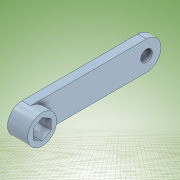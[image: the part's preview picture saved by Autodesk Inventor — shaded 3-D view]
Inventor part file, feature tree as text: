
AUTODESK INVENTOR PART (.ipt)
format: ipt  version: 2022 (Build 260153000, 153)  size: 145,408 bytes
history: native  units: mm
features: extrude x3, sketch x3, other x1
ambient origin geometry x8: Origin, YZ Plane, XZ Plane, XY Plane, X Axis, Y Axis, Z Axis, Center Point
bodies: Body1 (feature_tree)
feature tree (7):
  other  "Sólido1"
  extrude  "Extrusión1"  Depth=10.0mm
  extrude  "Extrusión2"  Depth=4.0mm
  extrude  "Extrusión3"  Depth=4.0mm TaperAngle=0.0deg
  sketch  "Boceto1"  dims[d1=10.0mm d2=10.0mm]
  sketch  "Boceto2"  dims[d3=40.0mm d4=4.0mm]
  sketch  "Boceto3"  dims[d5=3.0mm d6=0.0mm d8=4.0mm d9=0.0mm d10=6.1mm d11=6.8mm d12=0.0mm]
